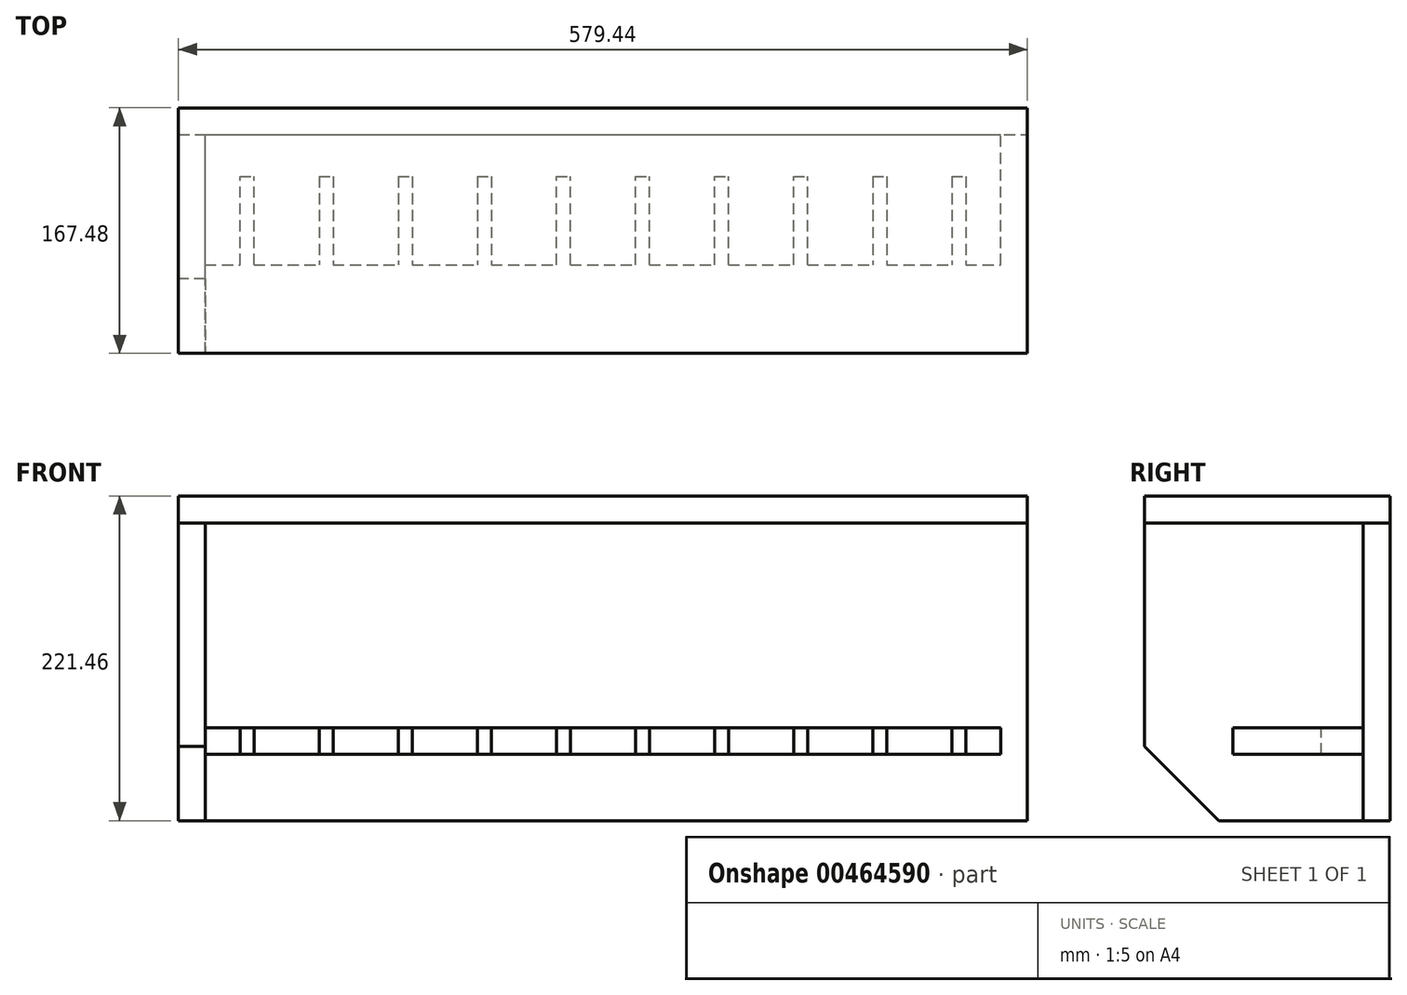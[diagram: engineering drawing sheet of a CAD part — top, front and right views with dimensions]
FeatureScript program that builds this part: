
annotation { "Feature Type Name" : "Feature", "Feature Type Description" : "" }
export const myFeature = defineFeature(function(context is Context, id is Id, definition is map)
    precondition{}
    {
        {
            var Q0;
            Q0=qCreatedBy(makeId("Front.planeOp"),FACE);
            var sketch = newSketch(context, id + "F0", { "sketchPlane" : qUnion([Q0])});
            skLineSegment(sketch, "E0.bottom", {"start": v(-289.72, 101.6) * mm, "end": v(289.72, 101.6) * mm});
            skLineSegment(sketch, "E0.top", {"start": v(-289.72, -101.6) * mm, "end": v(289.72, -101.6) * mm});
            skLineSegment(sketch, "E0.left", {"start": v(-289.72, 101.6) * mm, "end": v(-289.72, -101.6) * mm});
            skLineSegment(sketch, "E0.right", {"start": v(289.72, 101.6) * mm, "end": v(289.72, -101.6) * mm});
            skSolve(sketch);
        }
        {
            var Q0;
            Q0=makeQuery(id+"F0.imprint","IMPRINT",FACE,{"disambiguationData":[TD([[makeQuery(id+"F0.imprint","IMPRINT",EDGE,{"derivedFrom":sQuery(id+"F0.wireOp",EDGE,"E0.bottom")}),-1.0]])]});
            extrude(context, id + "F1", {"entities" : qUnion([Q0]), "oppositeDirection" : true, "depth" : 18.26 * mm});
        }
        {
            var Q0;
            Q0=makeQuery(id+"F1.opExtrude","CAP_FACE",FACE,{"disambiguationData":[OSD([sQuery(id+"F0.wireOp",EDGE,"E0.bottom"),sQuery(id+"F0.wireOp",EDGE,"E0.top"),sQuery(id+"F0.wireOp",EDGE,"E0.left"),sQuery(id+"F0.wireOp",EDGE,"E0.right")])],"isStart":true});
            var sketch = newSketch(context, id + "F2", { "sketchPlane" : qUnion([Q0])});
            skLineSegment(sketch, "E1.bottom", {"start": v(-289.72, 101.6) * mm, "end": v(-271.46, 101.6) * mm});
            skLineSegment(sketch, "E1.top", {"start": v(-289.72, -101.6) * mm, "end": v(-271.46, -101.6) * mm});
            skLineSegment(sketch, "E1.left", {"start": v(-289.72, 101.6) * mm, "end": v(-289.72, -101.6) * mm});
            skLineSegment(sketch, "E1.right", {"start": v(-271.46, 101.6) * mm, "end": v(-271.46, -101.6) * mm});
            skSolve(sketch);
        }
        {
            var Q0;
            Q0=makeQuery(id+"F2.imprint","IMPRINT",FACE,{"disambiguationData":[TD([[makeQuery(id+"F2.imprint","IMPRINT",EDGE,{"derivedFrom":sQuery(id+"F2.wireOp",EDGE,"E1.bottom")}),-1.0]])]});
            extrude(context, id + "F3", {"entities" : qUnion([Q0]), "depth" : 149.22 * mm});
        }
        {
            var Q0;
            Q0=makeQuery(id+"F3.opExtrude","SWEPT_FACE",FACE,{"disambiguationData":[OSD([sQuery(id+"F2.wireOp",EDGE,"E1.bottom")])]});
            var sketch = newSketch(context, id + "F4", { "sketchPlane" : qUnion([Q0])});
            skLineSegment(sketch, "E2.bottom", {"start": v(-289.72, 18.26) * mm, "end": v(289.72, 18.26) * mm});
            skLineSegment(sketch, "E2.top", {"start": v(-289.72, -149.23) * mm, "end": v(289.72, -149.23) * mm});
            skLineSegment(sketch, "E2.left", {"start": v(-289.72, 18.26) * mm, "end": v(-289.72, -149.23) * mm});
            skLineSegment(sketch, "E2.right", {"start": v(289.72, 18.26) * mm, "end": v(289.72, -149.23) * mm});
            skSolve(sketch);
        }
        {
            var Q0;
            Q0 = qSketchRegion(id + "F4", true);
            extrude(context, id + "F5", {"entities" : qUnion([Q0]), "depth" : 18.26 * mm});
        }
        {
            var Q0;
            Q0=makeQuery(id+"F1.opExtrude","CAP_FACE",FACE,{"disambiguationData":[OSD([sQuery(id+"F0.wireOp",EDGE,"E0.bottom"),sQuery(id+"F0.wireOp",EDGE,"E0.top"),sQuery(id+"F0.wireOp",EDGE,"E0.left"),sQuery(id+"F0.wireOp",EDGE,"E0.right")])],"isStart":true});
            var sketch = newSketch(context, id + "F6", { "sketchPlane" : qUnion([Q0])});
            skLineSegment(sketch, "E3.bottom", {"start": v(-271.46, -38.1) * mm, "end": v(271.46, -38.1) * mm});
            skLineSegment(sketch, "E3.top", {"start": v(-271.46, -56.36) * mm, "end": v(271.46, -56.36) * mm});
            skLineSegment(sketch, "E3.left", {"start": v(-271.46, -38.1) * mm, "end": v(-271.46, -56.36) * mm});
            skLineSegment(sketch, "E3.right", {"start": v(271.46, -38.1) * mm, "end": v(271.46, -56.36) * mm});
            skLineSegment(sketch, "E4", {"start": v(-271.46, 101.6) * mm, "end": v(-271.46, -101.6) * mm, "construction": true});
            skLineSegment(sketch, "E5", {"start": v(271.46, 101.6) * mm, "end": v(271.46, -101.6) * mm, "construction": true});
            skSolve(sketch);
        }
        {
            var Q0;
            Q0 = qSketchRegion(id + "F6", true);
            extrude(context, id + "F7", {"entities" : qUnion([Q0]), "depth" : 88.9 * mm});
        }
        {
            var Q0;
            Q0=makeQuery(id+"F7.opExtrude","SWEPT_FACE",FACE,{"disambiguationData":[OSD([sQuery(id+"F6.wireOp",EDGE,"E3.bottom")])]});
            var sketch = newSketch(context, id + "F8", { "sketchPlane" : qUnion([Q0])});
            skLineSegment(sketch, "E6.bottom", {"start": v(-247.65, -88.9) * mm, "end": v(-238.12, -88.9) * mm});
            skLineSegment(sketch, "E6.top", {"start": v(-247.65, -28.58) * mm, "end": v(-238.13, -28.58) * mm});
            skLineSegment(sketch, "E6.left", {"start": v(-247.65, -88.9) * mm, "end": v(-247.65, -28.58) * mm});
            skLineSegment(sketch, "E6.right", {"start": v(-238.13, -88.9) * mm, "end": v(-238.13, -28.58) * mm});
            skPoint(sketch, "E7", {"position": v(-242.89, -28.58) * mm});
            skLineSegment(sketch, "E8", {"start": v(-271.46, -28.58) * mm, "end": v(271.46, -28.58) * mm, "construction": true});
            skLineSegment(sketch, "E9.bottom", {"start": v(-193.68, -28.58) * mm, "end": v(-184.15, -28.58) * mm});
            skLineSegment(sketch, "E9.top", {"start": v(-193.68, -88.9) * mm, "end": v(-184.15, -88.9) * mm});
            skLineSegment(sketch, "E9.left", {"start": v(-193.68, -28.58) * mm, "end": v(-193.68, -88.9) * mm});
            skLineSegment(sketch, "E9.right", {"start": v(-184.15, -28.58) * mm, "end": v(-184.15, -88.9) * mm});
            skLineSegment(sketch, "E10.bottom", {"start": v(-139.7, -28.58) * mm, "end": v(-130.18, -28.58) * mm});
            skLineSegment(sketch, "E10.top", {"start": v(-139.7, -88.9) * mm, "end": v(-130.18, -88.9) * mm});
            skLineSegment(sketch, "E10.left", {"start": v(-139.7, -28.58) * mm, "end": v(-139.7, -88.9) * mm});
            skLineSegment(sketch, "E10.right", {"start": v(-130.18, -28.58) * mm, "end": v(-130.18, -88.9) * mm});
            skLineSegment(sketch, "E11.bottom", {"start": v(-85.73, -28.58) * mm, "end": v(-76.2, -28.58) * mm});
            skLineSegment(sketch, "E11.top", {"start": v(-85.73, -88.9) * mm, "end": v(-76.2, -88.9) * mm});
            skLineSegment(sketch, "E11.left", {"start": v(-85.73, -28.58) * mm, "end": v(-85.73, -88.9) * mm});
            skLineSegment(sketch, "E11.right", {"start": v(-76.2, -28.58) * mm, "end": v(-76.2, -88.9) * mm});
            skLineSegment(sketch, "E12.bottom", {"start": v(-31.75, -88.9) * mm, "end": v(-22.23, -88.9) * mm});
            skLineSegment(sketch, "E12.top", {"start": v(-31.75, -28.58) * mm, "end": v(-22.23, -28.58) * mm});
            skLineSegment(sketch, "E12.left", {"start": v(-31.75, -88.9) * mm, "end": v(-31.75, -28.58) * mm});
            skLineSegment(sketch, "E12.right", {"start": v(-22.23, -88.9) * mm, "end": v(-22.23, -28.58) * mm});
            skLineSegment(sketch, "E13.bottom", {"start": v(22.22, -88.9) * mm, "end": v(31.75, -88.9) * mm});
            skLineSegment(sketch, "E13.top", {"start": v(22.22, -28.58) * mm, "end": v(31.75, -28.58) * mm});
            skLineSegment(sketch, "E13.left", {"start": v(22.22, -88.9) * mm, "end": v(22.22, -28.58) * mm});
            skLineSegment(sketch, "E13.right", {"start": v(31.75, -88.9) * mm, "end": v(31.75, -28.58) * mm});
            skLineSegment(sketch, "E14.bottom", {"start": v(76.2, -88.9) * mm, "end": v(85.72, -88.9) * mm});
            skLineSegment(sketch, "E14.top", {"start": v(76.2, -28.58) * mm, "end": v(85.72, -28.58) * mm});
            skLineSegment(sketch, "E14.left", {"start": v(76.2, -88.9) * mm, "end": v(76.2, -28.58) * mm});
            skLineSegment(sketch, "E14.right", {"start": v(85.72, -88.9) * mm, "end": v(85.72, -28.58) * mm});
            skLineSegment(sketch, "E15.bottom", {"start": v(130.17, -88.9) * mm, "end": v(139.7, -88.9) * mm});
            skLineSegment(sketch, "E15.top", {"start": v(130.17, -28.58) * mm, "end": v(139.7, -28.58) * mm});
            skLineSegment(sketch, "E15.left", {"start": v(130.17, -88.9) * mm, "end": v(130.17, -28.58) * mm});
            skLineSegment(sketch, "E15.right", {"start": v(139.7, -88.9) * mm, "end": v(139.7, -28.58) * mm});
            skLineSegment(sketch, "E16.bottom", {"start": v(184.15, -28.58) * mm, "end": v(193.67, -28.58) * mm});
            skLineSegment(sketch, "E16.top", {"start": v(184.15, -88.9) * mm, "end": v(193.67, -88.9) * mm});
            skLineSegment(sketch, "E16.left", {"start": v(184.15, -28.58) * mm, "end": v(184.15, -88.9) * mm});
            skLineSegment(sketch, "E16.right", {"start": v(193.67, -28.58) * mm, "end": v(193.67, -88.9) * mm});
            skLineSegment(sketch, "E17.bottom", {"start": v(238.12, -28.58) * mm, "end": v(247.65, -28.58) * mm});
            skLineSegment(sketch, "E17.top", {"start": v(238.12, -88.9) * mm, "end": v(247.65, -88.9) * mm});
            skLineSegment(sketch, "E17.left", {"start": v(238.12, -28.58) * mm, "end": v(238.12, -88.9) * mm});
            skLineSegment(sketch, "E17.right", {"start": v(247.65, -28.58) * mm, "end": v(247.65, -88.9) * mm});
            skSolve(sketch);
        }
        {
            var Q0;
            Q0 = qSketchRegion(id + "F8", true);
            extrude(context, id + "F9", {"entities" : qUnion([Q0]), "operationType" : NewBodyOperationType.REMOVE, "endBound" : BoundingType.THROUGH_ALL, "oppositeDirection" : true, "depth" : 25.4 * mm});
        }
        {
            var Q0;
            Q0=makeQuery(id+"F3.opExtrude","SWEPT_FACE",FACE,{"disambiguationData":[OSD([sQuery(id+"F2.wireOp",EDGE,"E1.left")])]});
            var sketch = newSketch(context, id + "F10", { "sketchPlane" : qUnion([Q0])});
            skLineSegment(sketch, "E18", {"start": v(149.23, -50.8) * mm, "end": v(98.43, -101.6) * mm});
            skLineSegment(sketch, "E19", {"start": v(98.43, -101.6) * mm, "end": v(149.23, -101.6) * mm});
            skLineSegment(sketch, "E20", {"start": v(149.23, -101.6) * mm, "end": v(149.23, -50.8) * mm});
            skSolve(sketch);
        }
        {
            var Q0;
            Q0=makeQuery(id+"F10.imprint","IMPRINT",FACE,{"disambiguationData":[TD([[makeQuery(id+"F10.imprint","IMPRINT",EDGE,{"derivedFrom":sQuery(id+"F10.wireOp",EDGE,"E18")}),1.0]])]});
            extrude(context, id + "F11", {"entities" : qUnion([Q0]), "operationType" : NewBodyOperationType.REMOVE, "oppositeDirection" : true, "depth" : 25.4 * mm});
        }
    });
